# Revit family: Blucher_PlumbingFixture_GravityRoofDrain_402.104a
name_source: partatom
category: Plumbing Fixtures
revit_build: Autodesk Revit 2017 (Build: 20190508_0315(x64)
units: mm (PartAtom-declared; Revit-internal decimal feet)

## family parameters
Cut with Voids When Loaded = No
Host = Face
OmniClass Number = 23.70.50.21.24
OmniClass Title = Waste Water Drains
Part Type = Normal
Room Calculation Point = No
Round Connector Dimension = Use Diameter
Shared = No

## types (4) — shared parameters
Assembly Code = D2040200
AssetType = Fixed
BIMObjectName = Blucher_PlumbingFixture_GravityRoofDrain_LowerPart_402.10
ClassificationName = Uniclass2015
ClassificationValue = Pr_65_50_35_37
Color = Stainless Steel
Default Elevation = 1219 mm
Description = Lower part for roof drain with single ply membrane.
DocumentationCertificates = https://www.bimstore.co
DocumentationInstallationGuide = https://www.bimstore.co
DocumentationLiterature = https://www.bimstore.co
DocumentationMaintenance = https://www.bimstore.co
DocumentationTechnical = https://www.bimstore.co
DrainMaterial = Blucher_Stainless Steel
DurationUnit = Years
ExpectedLife = 50
Finish = 2B - Pickled
Grade = AISI 304/EN 1.4301 or AISI 316L/EN 1.4404
IfcExportAs = IfcFlowTerminal
IfcExportType = IfcWasteTerminalTypeEnum.FLOORWASTE
Keynote = R10
Manufacturer = BLÜCHER
ManufacturerName = BLÜCHER
Material = Available in Stainless Steel AISI 304 & Stainless Steel AISI 316L
Model = BLÜCHER Lower Part For Roof Drain
ModelReference = BLÜCHER Lower Part For Roof Drain
NBSDescription = Gravity rainwater outlets
NBSObjectName = BLÜCHER - Gravity rainwater outlets
NBSReference = 90-10-20/302
NominalDepth = 280 mm  [stored 0.918635 ft]
NominalLength = 280 mm  [stored 0.918635 ft]
PipeAdjustment = 300 mm
ProductionYear = 2021
ReferencedStandard = EN1253
Shape = Rectangular
URL = http://www.blucher.com
WarrantyDurationUnit = Years
_BSBibleVersion = 15
_CurrentRevision = 1
_DistributedBy = www.bimstore.co.uk
zero-valued in all types: _BimSpecGuid

## per-type parameters (varying)
| type | D | ModelNumber | Size | Type Comments | TypeName |
| 110mm | 110 mm  [stored 0.360892 ft] | 402.004.110 | 280mm x 280mm x 110mm | 402.004.110 | 402.004.110 |
| 50mm | 50 mm  [stored 0.164042 ft] | 402.004.050 | 280mm x 280mm x 50mm | 402.004.050 | 402.004.050 |
| 75mm | 75 mm | 402.004.075 | 280mm x 280mm x 75mm | 402.004.075 | 402.004.075 |
| 40mm | 40 mm  [stored 0.131234 ft] | 402.004.040 | 280mm x 280mm x 40mm | 402.004.040 | 402.004.040 |

note: [stored X ft] marks values corroborated as IEEE doubles in the binary element streams (Revit-internal decimal feet)

## geometry (parser evidence)
native form markers: Blend x4, Sweep x14
no freeform markers — native parametric forms only
